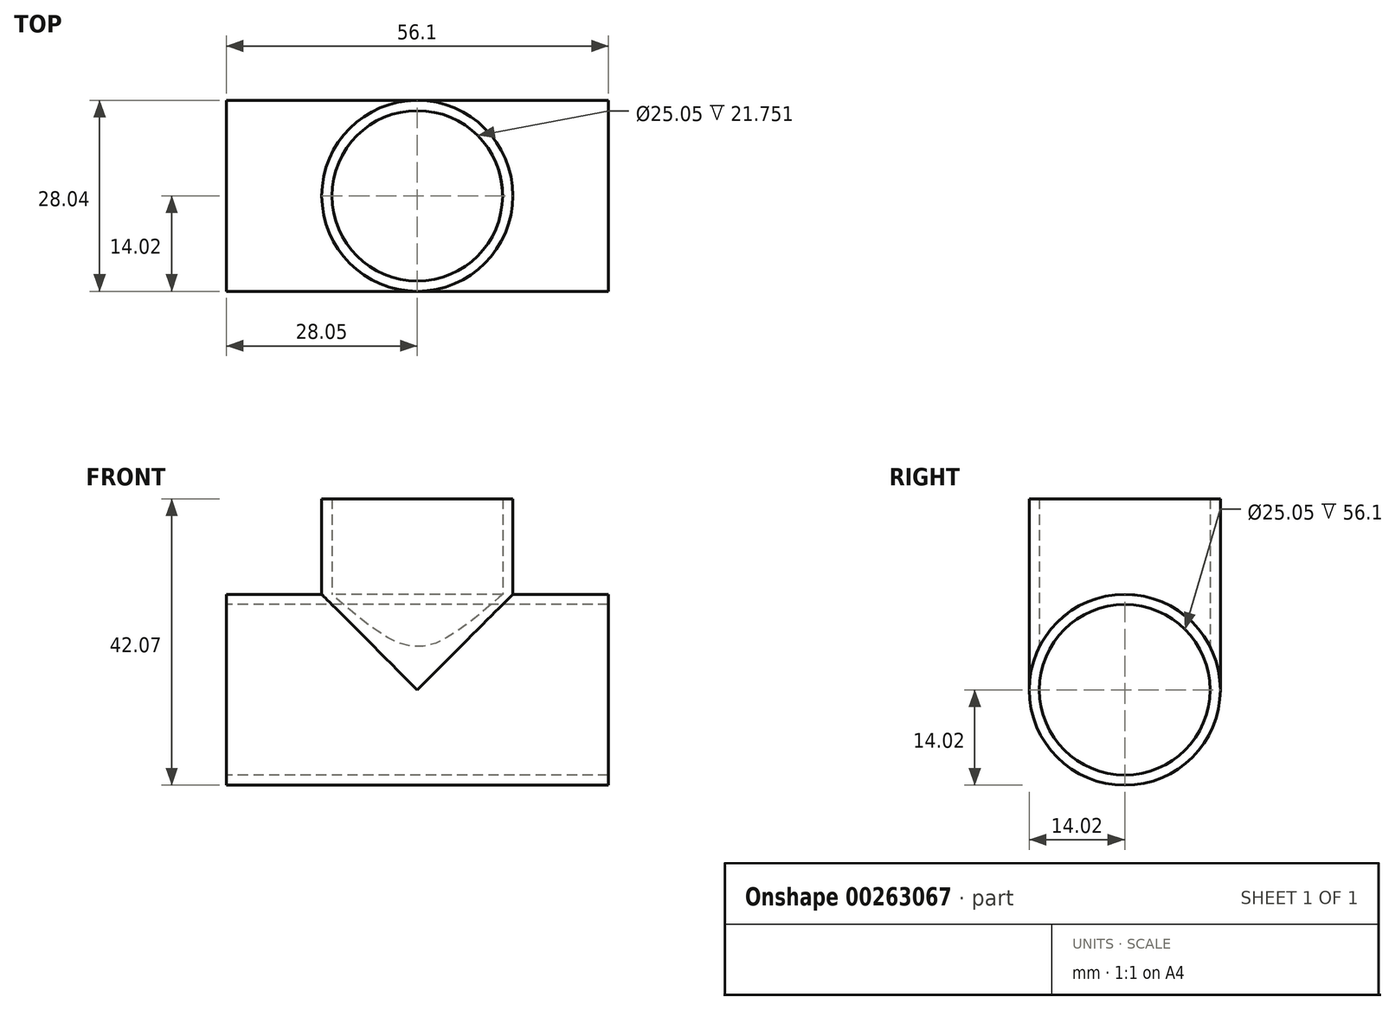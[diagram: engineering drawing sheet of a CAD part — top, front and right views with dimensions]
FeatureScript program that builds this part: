
annotation { "Feature Type Name" : "Feature", "Feature Type Description" : "" }
export const myFeature = defineFeature(function(context is Context, id is Id, definition is map)
    precondition{}
    {
        {
            var Q0;
            Q0=qCreatedBy(makeId("Right.planeOp"),FACE);
            var sketch = newSketch(context, id + "F0", { "sketchPlane" : qUnion([Q0])});
            skCircle(sketch, "E0", {"center": v(0, 0) * mm, "radius": 12.52 * mm});
            skCircle(sketch, "E1", {"center": v(0, 0) * mm, "radius": 14.02 * mm});
            skSolve(sketch);
        }
        {
            var Q0;
            Q0=makeQuery(id+"F0.imprint","IMPRINT",FACE,{"disambiguationData":[TD([[makeQuery(id+"F0.imprint","IMPRINT",EDGE,{"derivedFrom":sQuery(id+"F0.wireOp",EDGE,"E0")}),-1.0]])]});
            extrude(context, id + "F1", {"entities" : qUnion([Q0]), "endBound" : BoundingType.SYMMETRIC, "depth" : 56.1 * mm});
        }
        {
            var Q0;
            Q0=qCreatedBy(makeId("Top.planeOp"),FACE);
            var sketch = newSketch(context, id + "F2", { "sketchPlane" : qUnion([Q0])});
            skCircle(sketch, "E2", {"center": v(0, 0) * mm, "radius": 12.52 * mm});
            skCircle(sketch, "E3", {"center": v(0, 0) * mm, "radius": 14.02 * mm});
            skSolve(sketch);
        }
        {
            var Q0;
            Q0 = qSketchRegion(id + "F2", true);
            extrude(context, id + "F3", {"entities" : qUnion([Q0]), "operationType" : NewBodyOperationType.ADD, "depth" : 28.05 * mm});
        }
        {
            var Q0;
            Q0=makeQuery(id+"F0.imprint","IMPRINT",FACE,{"disambiguationData":[TD([[makeQuery(id+"F0.imprint","IMPRINT",EDGE,{"derivedFrom":sQuery(id+"F0.wireOp",EDGE,"E0")}),1.0]])]});
            extrude(context, id + "F4", {"entities" : qUnion([Q0]), "operationType" : NewBodyOperationType.REMOVE, "endBound" : BoundingType.SYMMETRIC, "oppositeDirection" : true, "depth" : 50.8 * mm});
        }
    });
